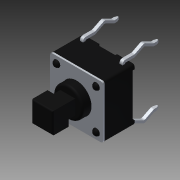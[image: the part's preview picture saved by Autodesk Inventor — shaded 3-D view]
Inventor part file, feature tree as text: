
AUTODESK INVENTOR PART (.ipt)
format: ipt  version: 2015 (Build 190159000, 159)  size: 372,736 bytes
history: native  units: in
note: dims shown in document units (in); Inventor stores cm internally (conversion verified against a paired STEP export)
features: imported_body x5, chamfer x3, other x2, fillet x1
ambient origin geometry x8: Origin, YZ Plane, XZ Plane, XY Plane, X Axis, Y Axis, Z Axis, Center Point
bodies: Body1 (feature_tree), Body2 (feature_tree), Body3 (feature_tree), Body4 (feature_tree), Body5 (feature_tree)
feature tree (11):
  other  "Cut-Revolve1[2]"
  other  "tactpushbutton1"
  fillet  "Fillet4"  [1 undecoded]
  chamfer  "Chamfer2"  [1 undecoded]
  chamfer  "Chamfer6"  [1 undecoded]
  chamfer  "Chamfer8"  [1 undecoded]
  imported_body  "Base1"
  imported_body  "Base2"
  imported_body  "Base3"
  imported_body  "Base4"
  imported_body  "Base5"
note: 4 required parameter values undecoded (feature->parameter linkage not recoverable at this tier; creation-order binding heuristic only, values carry confidence <= 0.55)
